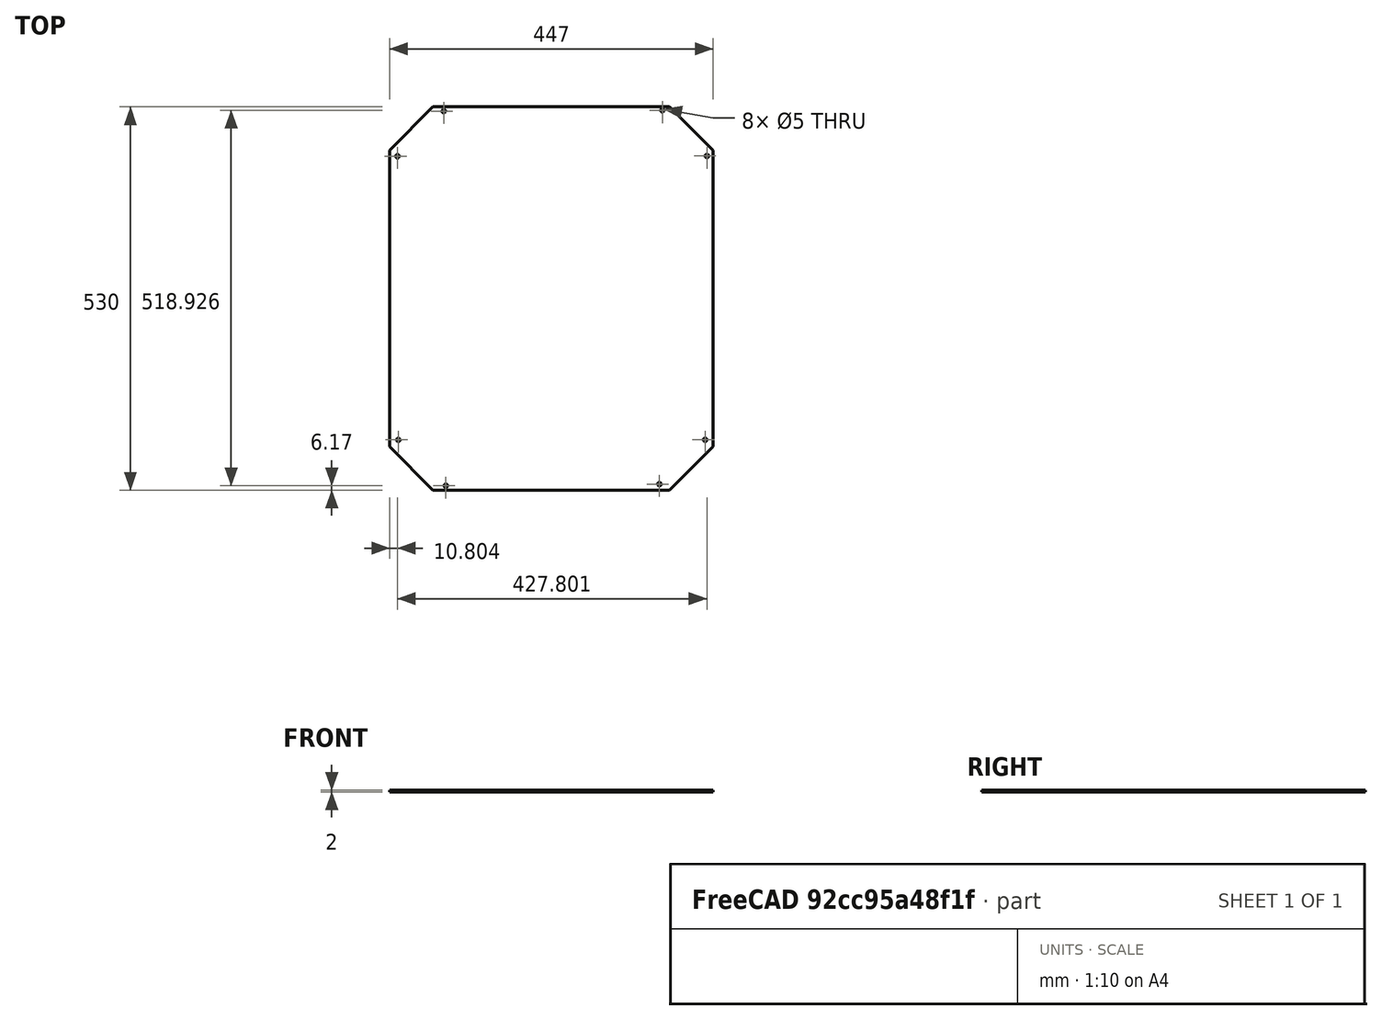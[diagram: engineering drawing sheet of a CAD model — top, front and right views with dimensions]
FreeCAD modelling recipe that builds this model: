
FCSTD DOCUMENT  (FreeCAD 0.16R6698 (Git))
Label: Plaque latéral switch
License: All rights reserved
LicenseURL: http://en.wikipedia.org/wiki/All_rights_reserved
objects: Sketcher::SketchObject×1, PartDesign::Pad×1
note: 3 computed .brp shape members not serialized (recipe doc carries the construction recipe); baked Part::Feature solids carry a one-line shape summary decoded from their .brp

FEATURE [Sketcher::SketchObject] Sketch
  sketch-geometry (16):
    g0: LineSegment StartX=-171.234 StartY=259.917 StartZ=0 EndX=155.766 EndY=259.917 EndZ=0
    g1: LineSegment StartX=155.766 StartY=259.917 StartZ=0 EndX=215.766 EndY=199.917 EndZ=0
    g2: LineSegment StartX=215.766 StartY=199.917 StartZ=0 EndX=215.766 EndY=-210.083 EndZ=0
    g3: LineSegment StartX=215.766 StartY=-210.083 StartZ=0 EndX=155.766 EndY=-270.083 EndZ=0
    g4: LineSegment StartX=155.766 StartY=-270.083 StartZ=0 EndX=-171.234 EndY=-270.083 EndZ=0
    g5: LineSegment StartX=-171.234 StartY=-270.083 StartZ=0 EndX=-231.234 EndY=-210.083 EndZ=0
    g6: LineSegment StartX=-231.234 StartY=-210.083 StartZ=0 EndX=-231.234 EndY=199.917 EndZ=0
    g7: LineSegment StartX=-231.234 StartY=199.917 StartZ=0 EndX=-171.234 EndY=259.917 EndZ=0
    g8: Circle CenterX=-220.426 CenterY=191.552 CenterZ=0 NormalX=0 NormalY=0 NormalZ=1 Radius=2.5
    g9: Circle CenterX=-156.405 CenterY=253.931 CenterZ=0 NormalX=0 NormalY=0 NormalZ=1 Radius=2.5
    g10: Circle CenterX=145.683 CenterY=255.016 CenterZ=0 NormalX=0 NormalY=0 NormalZ=1 Radius=2.5
    g11: Circle CenterX=-219.195 CenterY=-200.608 CenterZ=0 NormalX=0 NormalY=0 NormalZ=1 Radius=2.5
    g12: Circle CenterX=-153.602 CenterY=-263.91 CenterZ=0 NormalX=0 NormalY=0 NormalZ=1 Radius=2.5
    g13: Circle CenterX=141.603 CenterY=-261.7 CenterZ=0 NormalX=0 NormalY=0 NormalZ=1 Radius=2.5
    g14: Circle CenterX=204.926 CenterY=-200.477 CenterZ=0 NormalX=0 NormalY=0 NormalZ=1 Radius=2.5
    g15: Circle CenterX=207.375 CenterY=191.908 CenterZ=0 NormalX=0 NormalY=0 NormalZ=1 Radius=2.5
  constraints (27):
    c: Horizontal(g0)
    c: Coincident(g0,g1)
    c: Coincident(g1,g2)
    c: Vertical(g2)
    c: Coincident(g2,g3)
    c: Coincident(g3,g4)
    c: Horizontal(g4)
    c: Coincident(g4,g5)
    c: Coincident(g5,g6)
    c: Vertical(g6)
    c: Coincident(g6,g7)
    c: Coincident(g7,g0)
    c: DistanceY(g7,g7) = 60
    c: DistanceX(g1,g1) = 60
    c: DistanceX(g5,g5) = 60
    c: DistanceY(g5,g5) = 60
    c: DistanceY(g3,g3) = 60
    c: DistanceY(g1,g1) = 60
    c: DistanceX(g3,g3) = 60
    c: Radius(g15) = 2.5
    c: Equal(g15,g10)
    c: Equal(g15,g9)
    c: Equal(g15,g8)
    c: Equal(g15, g11-g14) x4
    c: DistanceX(g6,g0) = 60
    c: DistanceX(g0,g0) = 327
    c: DistanceY(g6,g6) = 410
FEATURE [PartDesign::Pad] Pad
  Length = 2
  Length2 = 100
  Sketch = -> Sketch
  Type = 0
